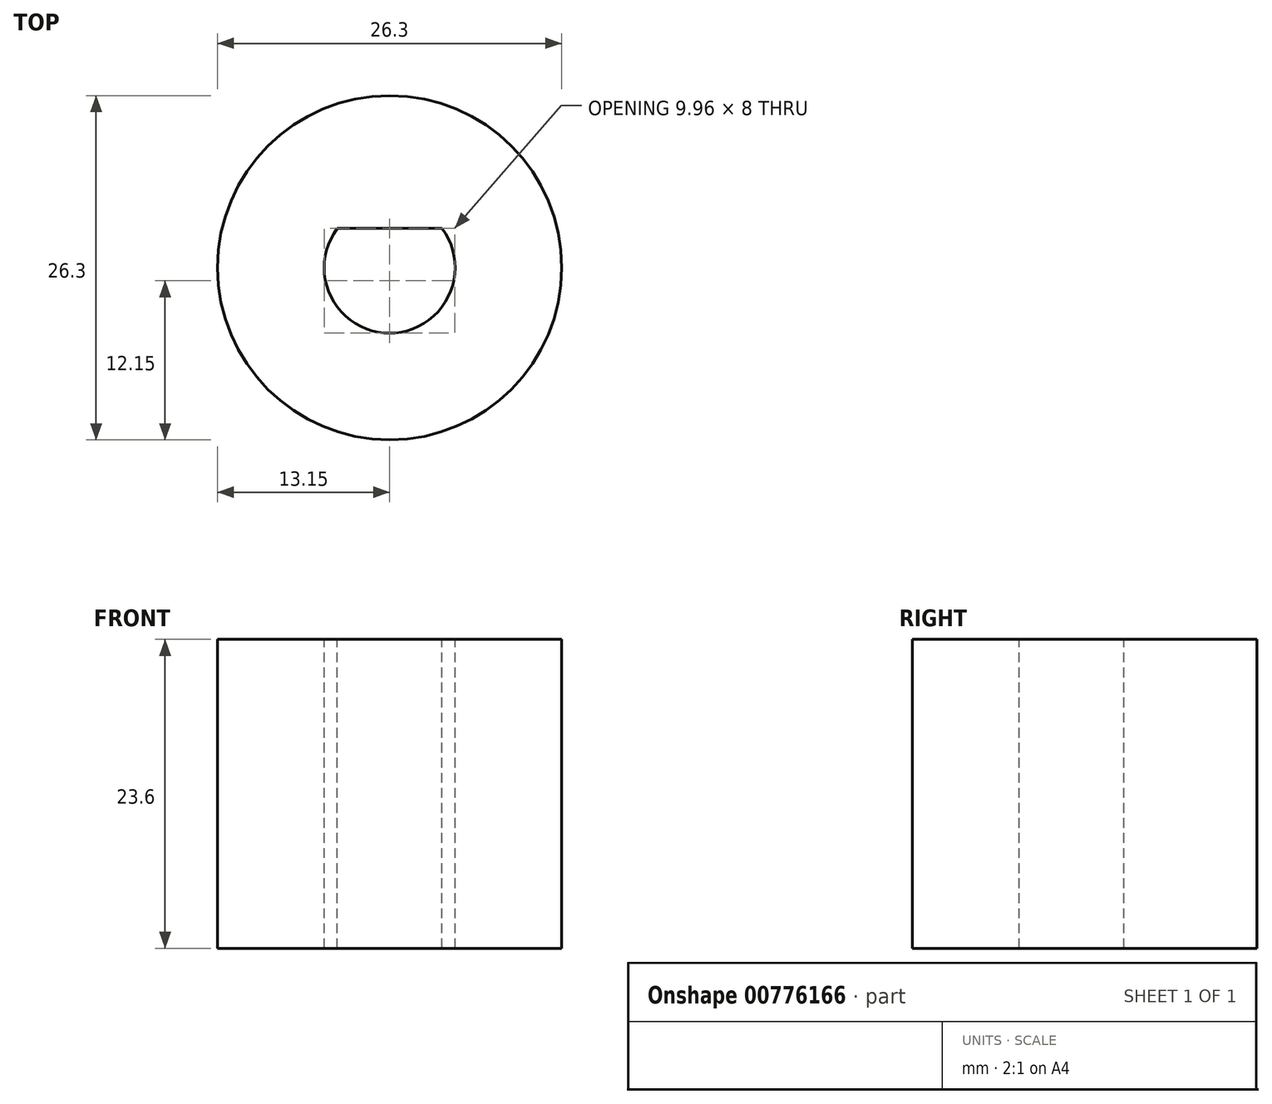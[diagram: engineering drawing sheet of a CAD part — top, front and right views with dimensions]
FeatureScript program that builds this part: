
annotation { "Feature Type Name" : "Feature", "Feature Type Description" : "" }
export const myFeature = defineFeature(function(context is Context, id is Id, definition is map)
    precondition{}
    {
        {
            var Q0;
            Q0=qCreatedBy(makeId("Top.planeOp"),FACE);
            var sketch = newSketch(context, id + "F0", { "sketchPlane" : qUnion([Q0])});
            skCircle(sketch, "E0", {"center": v(0, 0) * mm, "radius": 13.15 * mm});
            skSolve(sketch);
        }
        {
            var Q0;
            Q0=makeQuery(id+"F0.imprint","IMPRINT",FACE,{"disambiguationData":[TD([[makeQuery(id+"F0.imprint","IMPRINT",EDGE,{"derivedFrom":sQuery(id+"F0.wireOp",EDGE,"E0")}),1.0]])]});
            var sketch = newSketch(context, id + "F1", { "sketchPlane" : qUnion([Q0])});
            skCircle(sketch, "E1", {"center": v(0, 0) * mm, "radius": 5 * mm});
            skLineSegment(sketch, "E2", {"start": v(0, 3) * mm, "end": v(-4, 3) * mm});
            skLineSegment(sketch, "E3", {"start": v(0, 3) * mm, "end": v(4, 3) * mm});
            skSolve(sketch);
        }
        {
            var Q0;
            Q0 = qSketchRegion(id + "F0", true);
            extrude(context, id + "F2", {"entities" : qUnion([Q0]), "oppositeDirection" : true, "depth" : 23.6 * mm, "offsetDistance" : 25.4 * mm});
        }
        {
            var Q0;
            {var subQ0=sQuery(id+"F1.wireOp",EDGE,"E2");Q0=makeQuery(id+"F1.imprint","IMPRINT",FACE,{"disambiguationData":[TD([[makeQuery(id+"F1.imprint","IMPRINT",EDGE,{"derivedFrom":subQ0}),1.0]])]});}
            var sketch = newSketch(context, id + "F3", { "sketchPlane" : qUnion([Q0])});
            skSolve(sketch);
        }
        {
            var Q0;
            {var subQ0=sQuery(id+"F1.wireOp",EDGE,"E2");Q0=makeQuery(id+"F3.imprint","IMPRINT",FACE,{"disambiguationData":[TD([[makeQuery(id+"F3.imprint","IMPRINT",EDGE,{"derivedFrom":makeQuery(id+"F1.imprint","IMPRINT",EDGE,{"derivedFrom":subQ0})}),1.0]])]});}
            extrude(context, id + "F4", {"entities" : qUnion([Q0]), "operationType" : NewBodyOperationType.REMOVE, "oppositeDirection" : true, "depth" : 25.4 * mm, "offsetDistance" : 25.4 * mm});
        }
    });
